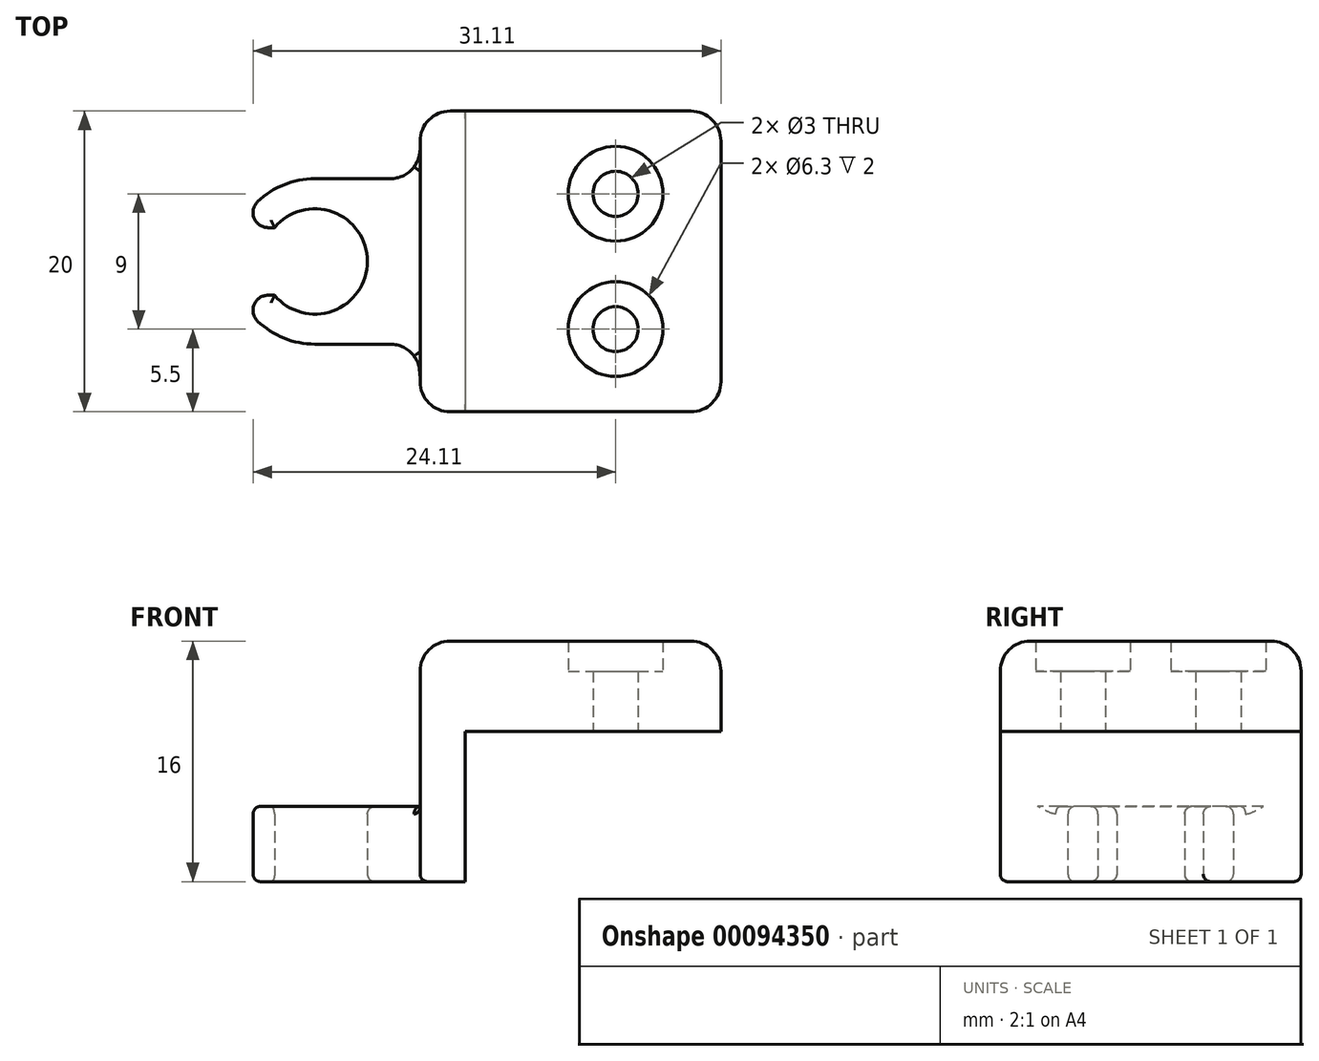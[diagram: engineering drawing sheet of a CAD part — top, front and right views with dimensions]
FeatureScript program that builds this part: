
annotation { "Feature Type Name" : "Feature", "Feature Type Description" : "" }
export const myFeature = defineFeature(function(context is Context, id is Id, definition is map)
    precondition{}
    {
        {
            var Q0;
            Q0=qCreatedBy(makeId("Top.planeOp"),FACE);
            var sketch = newSketch(context, id + "F0", { "sketchPlane" : qUnion([Q0])});
            skCircle(sketch, "E0", {"center": v(0, 0) * mm, "radius": 3.5 * mm});
            skCircle(sketch, "E1", {"center": v(0, 0) * mm, "radius": 5.5 * mm});
            skLineSegment(sketch, "E2", {"start": v(-5.02, 2.25) * mm, "end": v(-2.68, 2.25) * mm});
            skLineSegment(sketch, "E3", {"start": v(-2.68, -2.25) * mm, "end": v(-5.02, -2.25) * mm});
            skLineSegment(sketch, "E4", {"start": v(0, 5.5) * mm, "end": v(7, 5.5) * mm});
            skLineSegment(sketch, "E5", {"start": v(0, -5.5) * mm, "end": v(7, -5.5) * mm});
            skLineSegment(sketch, "E6", {"start": v(7, -5.5) * mm, "end": v(7, 5.5) * mm});
            skLineSegment(sketch, "E7.bottom", {"start": v(7, 10) * mm, "end": v(10, 10) * mm});
            skLineSegment(sketch, "E7.top", {"start": v(7, -10) * mm, "end": v(10, -10) * mm});
            skLineSegment(sketch, "E7.left", {"start": v(7, 10) * mm, "end": v(7, -10) * mm});
            skLineSegment(sketch, "E7.right", {"start": v(10, 10) * mm, "end": v(10, -10) * mm});
            skPoint(sketch, "E8", {"position": v(10, 0) * mm});
            skSolve(sketch);
        }
        {
            var Q0;
            {var subQ0=sQuery(id+"F0.wireOp",EDGE,"E2");Q0=makeQuery(id+"F0.imprint","IMPRINT",FACE,{"disambiguationData":[TD([[makeQuery(id+"F0.imprint","IMPRINT",EDGE,{"derivedFrom":subQ0}),1.0]])]});}
            var Q1;
            {var subQ0=sQuery(id+"F0.wireOp",EDGE,"E4");Q1=makeQuery(id+"F0.imprint","IMPRINT",FACE,{"disambiguationData":[TD([[makeQuery(id+"F0.imprint","IMPRINT",EDGE,{"derivedFrom":subQ0}),-1.0]])]});}
            var Q2;
            {var subQ3=sQuery(id+"F0.wireOp",EDGE,"E7.bottom");Q2=makeQuery(id+"F0.imprint","IMPRINT",FACE,{"disambiguationData":[TD([[makeQuery(id+"F0.imprint","IMPRINT",EDGE,{"derivedFrom":subQ3}),-1.0]])]});}
            extrude(context, id + "F1", {"entities" : qUnion([Q0, Q1, Q2]), "depth" : 5 * mm});
        }
        {
            var Q0;
            Q0=makeQuery(id+"F1.opExtrude","CAP_FACE",FACE,{"disambiguationData":[OSD([sQuery(id+"F0.wireOp",EDGE,"E0"),sQuery(id+"F0.wireOp",EDGE,"E1"),sQuery(id+"F0.wireOp",EDGE,"E2"),sQuery(id+"F0.wireOp",EDGE,"E3"),sQuery(id+"F0.wireOp",EDGE,"E4"),sQuery(id+"F0.wireOp",EDGE,"E5"),sQuery(id+"F0.wireOp",EDGE,"E7.bottom"),sQuery(id+"F0.wireOp",EDGE,"E7.top"),sQuery(id+"F0.wireOp",EDGE,"E7.left"),sQuery(id+"F0.wireOp",EDGE,"E7.right")])],"isStart":false});
            var sketch = newSketch(context, id + "F2", { "sketchPlane" : qUnion([Q0])});
            skLineSegment(sketch, "E9", {"start": v(7, 5.5) * mm, "end": v(7, -5.5) * mm});
            skSolve(sketch);
        }
        {
            var Q0;
            Q0=makeQuery(id+"F2.imprint","IMPRINT",FACE,{"disambiguationData":[TD([[makeQuery(id+"F2.imprint","IMPRINT",EDGE,{"derivedFrom":sQuery(id+"F2.wireOp",EDGE,"E9")}),1.0]])]});
            extrude(context, id + "F3", {"entities" : qUnion([Q0]), "operationType" : NewBodyOperationType.ADD, "depth" : 5 * mm});
        }
        {
            var Q0;
            Q0=makeQuery(id+"F3.opExtrude","CAP_FACE",FACE,{"disambiguationData":[OSD([sQuery(id+"F0.wireOp",EDGE,"E7.bottom"),sQuery(id+"F0.wireOp",EDGE,"E7.top"),sQuery(id+"F0.wireOp",EDGE,"E7.left"),sQuery(id+"F0.wireOp",EDGE,"E7.right"),sQuery(id+"F2.wireOp",EDGE,"E9")])],"isStart":false});
            var sketch = newSketch(context, id + "F4", { "sketchPlane" : qUnion([Q0])});
            skLineSegment(sketch, "E10.bottom", {"start": v(7, 10) * mm, "end": v(27, 10) * mm});
            skLineSegment(sketch, "E10.top", {"start": v(7, -10) * mm, "end": v(27, -10) * mm});
            skLineSegment(sketch, "E10.left", {"start": v(7, 10) * mm, "end": v(7, -10) * mm});
            skLineSegment(sketch, "E10.right", {"start": v(27, 10) * mm, "end": v(27, -10) * mm});
            skSolve(sketch);
        }
        {
            var Q0;
            {var subQ2=sQuery(id+"F4.wireOp",EDGE,"E10.right");Q0=makeQuery(id+"F4.imprint","IMPRINT",FACE,{"disambiguationData":[TD([[makeQuery(id+"F4.imprint","IMPRINT",EDGE,{"derivedFrom":subQ2}),-1.0]])]});}
            var Q1;
            {var subQ0=sQuery(id+"F4.wireOp",EDGE,"E10.left");Q1=makeQuery(id+"F4.imprint","IMPRINT",FACE,{"disambiguationData":[TD([[makeQuery(id+"F4.imprint","IMPRINT",EDGE,{"derivedFrom":subQ0}),1.0]])]});}
            extrude(context, id + "F5", {"entities" : qUnion([Q0, Q1]), "operationType" : NewBodyOperationType.ADD, "depth" : 6 * mm});
        }
        {
            var Q0;
            Q0=makeQuery(id+"F3.opExtrude","CAP_EDGE",EDGE,{"disambiguationData":[OSD([sQuery(id+"F0.wireOp",EDGE,"E7.left"),sQuery(id+"F2.wireOp",EDGE,"E9")])],"isStart":true});
            var Q1;
            Q1=makeQuery(id+"F1.opExtrude","SWEPT_EDGE",EDGE,{"disambiguationData":[OSD([sQuery(id+"F0.wireOp",EDGE,"E5"),sQuery(id+"F0.wireOp",EDGE,"E7.left")])]});
            var Q2;
            Q2=makeQuery(id+"F1.opExtrude","SWEPT_EDGE",EDGE,{"disambiguationData":[OSD([sQuery(id+"F0.wireOp",EDGE,"E4"),sQuery(id+"F0.wireOp",EDGE,"E7.left")])]});
            var Q3;
            {var subQ0=sQuery(id+"F0.wireOp",EDGE,"E7.left");var subQ1=sQuery(id+"F0.wireOp",EDGE,"E7.top");Q3=makeQuery(id+"F5.boolean.opBoolean","MERGE",EDGE,{"derivedFrom":[makeQuery(id+"F3.boolean.opBoolean","MERGE",EDGE,{"derivedFrom":[makeQuery(id+"F1.opExtrude","SWEPT_EDGE",EDGE,{"disambiguationData":[OSD([subQ1,subQ0])]}),makeQuery(id+"F3.opExtrude","SWEPT_EDGE",EDGE,{"disambiguationData":[OSD([subQ1,subQ0])]})]}),makeQuery(id+"F5.opExtrude","SWEPT_EDGE",EDGE,{"disambiguationData":[OSD([sQuery(id+"F4.wireOp",EDGE,"E10.top"),sQuery(id+"F4.wireOp",EDGE,"E10.left")])]})]});}
            var Q4;
            {var subQ0=sQuery(id+"F0.wireOp",EDGE,"E7.left");var subQ1=sQuery(id+"F0.wireOp",EDGE,"E7.bottom");Q4=makeQuery(id+"F5.boolean.opBoolean","MERGE",EDGE,{"derivedFrom":[makeQuery(id+"F3.boolean.opBoolean","MERGE",EDGE,{"derivedFrom":[makeQuery(id+"F1.opExtrude","SWEPT_EDGE",EDGE,{"disambiguationData":[OSD([subQ1,subQ0])]}),makeQuery(id+"F3.opExtrude","SWEPT_EDGE",EDGE,{"disambiguationData":[OSD([subQ1,subQ0])]})]}),makeQuery(id+"F5.opExtrude","SWEPT_EDGE",EDGE,{"disambiguationData":[OSD([sQuery(id+"F4.wireOp",EDGE,"E10.bottom"),sQuery(id+"F4.wireOp",EDGE,"E10.left")])]})]});}
            var Q5;
            Q5=makeQuery(id+"F5.opExtrude","CAP_EDGE",EDGE,{"disambiguationData":[OSD([sQuery(id+"F4.wireOp",EDGE,"E10.left")])],"isStart":false});
            var Q6;
            Q6=makeQuery(id+"F5.opExtrude","CAP_EDGE",EDGE,{"disambiguationData":[OSD([sQuery(id+"F4.wireOp",EDGE,"E10.top")])],"isStart":false});
            var Q7;
            Q7=makeQuery(id+"F5.opExtrude","CAP_EDGE",EDGE,{"disambiguationData":[OSD([sQuery(id+"F4.wireOp",EDGE,"E10.right")])],"isStart":false});
            var Q8;
            Q8=makeQuery(id+"F5.opExtrude","CAP_EDGE",EDGE,{"disambiguationData":[OSD([sQuery(id+"F4.wireOp",EDGE,"E10.bottom")])],"isStart":false});
            var Q9;
            Q9=makeQuery(id+"F5.opExtrude","SWEPT_EDGE",EDGE,{"disambiguationData":[OSD([sQuery(id+"F4.wireOp",EDGE,"E10.bottom"),sQuery(id+"F4.wireOp",EDGE,"E10.right")])]});
            var Q10;
            Q10=makeQuery(id+"F5.opExtrude","SWEPT_EDGE",EDGE,{"disambiguationData":[OSD([sQuery(id+"F4.wireOp",EDGE,"E10.top"),sQuery(id+"F4.wireOp",EDGE,"E10.right")])]});
            fillet(context, id + "F6", {"entities" : qUnion([Q0, Q1, Q2, Q3, Q4, Q5, Q6, Q7, Q8, Q9, Q10]), "radius" : 2 * mm, "tangentPropagation" : true, "allowEdgeOverflow" : false});
        }
        {
            var Q0;
            Q0=makeQuery(id+"F1.opExtrude","SWEPT_EDGE",EDGE,{"disambiguationData":[OSD([sQuery(id+"F0.wireOp",EDGE,"E1"),sQuery(id+"F0.wireOp",EDGE,"E2")])]});
            var Q1;
            Q1=makeQuery(id+"F1.opExtrude","SWEPT_EDGE",EDGE,{"disambiguationData":[OSD([sQuery(id+"F0.wireOp",EDGE,"E1"),sQuery(id+"F0.wireOp",EDGE,"E3")])]});
            fillet(context, id + "F7", {"entities" : qUnion([Q0, Q1]), "radius" : 1 * mm, "tangentPropagation" : true, "allowEdgeOverflow" : false});
        }
        {
            var Q0;
            Q0=makeQuery(id+"F5.opExtrude","CAP_FACE",FACE,{"disambiguationData":[OSD([sQuery(id+"F4.wireOp",EDGE,"E10.bottom"),sQuery(id+"F4.wireOp",EDGE,"E10.top"),sQuery(id+"F4.wireOp",EDGE,"E10.left"),sQuery(id+"F4.wireOp",EDGE,"E10.right")])],"isStart":false});
            var sketch = newSketch(context, id + "F8", { "sketchPlane" : qUnion([Q0])});
            skPoint(sketch, "E11", {"position": v(20, 4.5) * mm});
            skPoint(sketch, "E11.positionSnap0", {"position": v(17, 8) * mm});
            skPoint(sketch, "E12", {"position": v(20, -4.5) * mm});
            skSolve(sketch);
        }
        {
            var Q0;
            Q0=sQuery(id+"F8.wireOp",VERTEX,"E11");
            var Q1;
            Q1=sQuery(id+"F8.wireOp",VERTEX,"E12");
            var Q2;
            Q2=makeQuery(id+"F1.opExtrude","SWEPT_BODY",BODY,{"disambiguationData":[OSD([sQuery(id+"F0.wireOp",EDGE,"E0"),sQuery(id+"F0.wireOp",EDGE,"E1"),sQuery(id+"F0.wireOp",EDGE,"E2"),sQuery(id+"F0.wireOp",EDGE,"E3"),sQuery(id+"F0.wireOp",EDGE,"E4"),sQuery(id+"F0.wireOp",EDGE,"E5"),sQuery(id+"F0.wireOp",EDGE,"E7.bottom"),sQuery(id+"F0.wireOp",EDGE,"E7.top"),sQuery(id+"F0.wireOp",EDGE,"E7.left"),sQuery(id+"F0.wireOp",EDGE,"E7.right")])]});
            hole(context, id + "F9", {"style" : HoleStyle.C_BORE, "endStyle" : HoleEndStyle.BLIND, "holeDiameter" : 3 * mm, "cBoreDiameter" : 6.3 * mm, "cBoreDepth" : 2 * mm, "holeDepth" : 10 * mm, "tappedDepth" : 12 * mm, "tapClearance" : 3, "locations" : qUnion([Q0, Q1]), "scope" : qUnion([Q2]), "startStyle" : HoleStartStyle.SKETCH});
        }
        {
            var Q0;
            Q0=makeQuery(id+"F1.opExtrude","CAP_EDGE",EDGE,{"disambiguationData":[OSD([sQuery(id+"F0.wireOp",EDGE,"E4")])],"isStart":false});
            var Q1;
            Q1=makeQuery(id+"F1.opExtrude","CAP_EDGE",EDGE,{"disambiguationData":[OSD([sQuery(id+"F0.wireOp",EDGE,"E5")])],"isStart":false});
            var Q2;
            Q2=makeQuery(id+"F1.opExtrude","CAP_EDGE",EDGE,{"disambiguationData":[OSD([sQuery(id+"F0.wireOp",EDGE,"E0")])],"isStart":false});
            var Q3;
            {var subQ0=sQuery(id+"F0.wireOp",EDGE,"E1");Q3=makeQuery(id+"F1.opExtrude","CAP_EDGE",EDGE,{"disambiguationData":[OSD([subQ0]),TDD([makeQuery(id+"F0.imprint","IMPRINT",EDGE,{"disambiguationData":[TD([[makeQuery(id+"F0.imprint","INTERSECT",VERTEX,{"derivedFrom":[subQ0,sQuery(id+"F0.wireOp",EDGE,"E3")]}),-1.0]])],"derivedFrom":subQ0})])],"isStart":true});}
            var Q4;
            Q4=makeQuery(id+"F1.opExtrude","CAP_EDGE",EDGE,{"disambiguationData":[OSD([sQuery(id+"F0.wireOp",EDGE,"E0")])],"isStart":true});
            var Q5;
            {var subQ0=sQuery(id+"F0.wireOp",EDGE,"E1");Q5=makeQuery(id+"F1.opExtrude","CAP_EDGE",EDGE,{"disambiguationData":[OSD([subQ0]),TDD([makeQuery(id+"F0.imprint","IMPRINT",EDGE,{"disambiguationData":[TD([[makeQuery(id+"F0.imprint","INTERSECT",VERTEX,{"derivedFrom":[subQ0,sQuery(id+"F0.wireOp",EDGE,"E2")]}),1.0]])],"derivedFrom":subQ0})])],"isStart":true});}
            fillet(context, id + "F10", {"entities" : qUnion([Q0, Q1, Q2, Q3, Q4, Q5]), "radius" : 0.5 * mm, "tangentPropagation" : true, "allowEdgeOverflow" : false});
        }
    });
